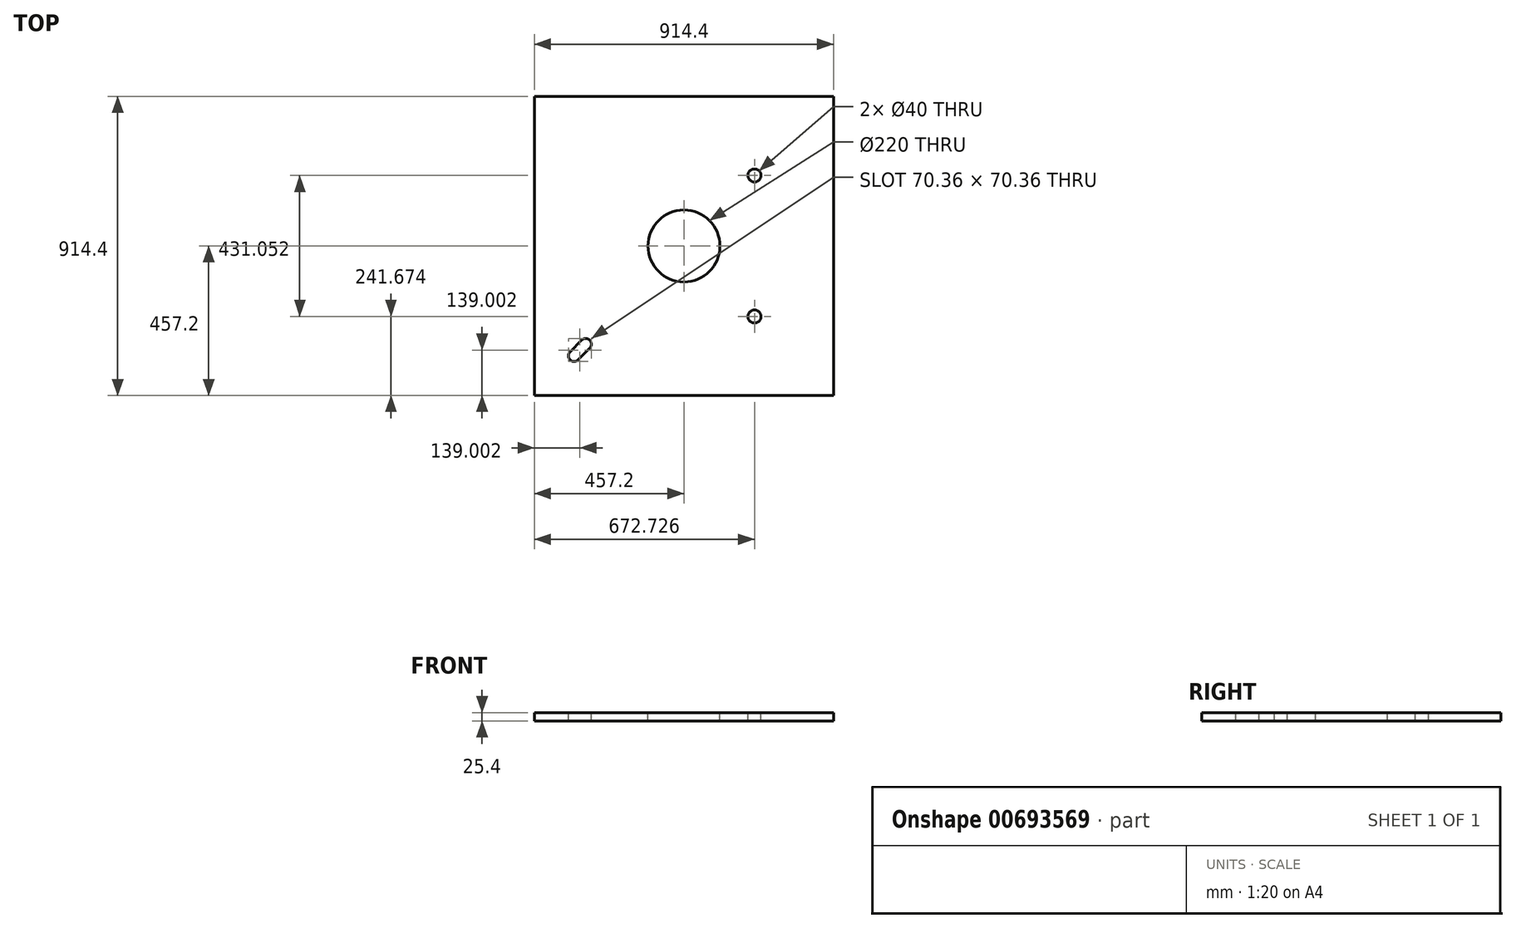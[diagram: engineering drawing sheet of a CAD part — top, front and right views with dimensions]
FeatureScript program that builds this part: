
annotation { "Feature Type Name" : "Feature", "Feature Type Description" : "" }
export const myFeature = defineFeature(function(context is Context, id is Id, definition is map)
    precondition{}
    {
        {
            var Q0;
            Q0=qCreatedBy(makeId("Top.planeOp"),FACE);
            var sketch = newSketch(context, id + "F0", { "sketchPlane" : qUnion([Q0])});
            skLineSegment(sketch, "E0.bottom", {"start": v(-457.2, 457.2) * mm, "end": v(457.2, 457.2) * mm});
            skLineSegment(sketch, "E0.top", {"start": v(-457.2, -457.2) * mm, "end": v(457.2, -457.2) * mm});
            skLineSegment(sketch, "E0.left", {"start": v(-457.2, 457.2) * mm, "end": v(-457.2, -457.2) * mm});
            skLineSegment(sketch, "E0.right", {"start": v(457.2, 457.2) * mm, "end": v(457.2, -457.2) * mm});
            skPoint(sketch, "E0.middle", {"position": v(0, 0) * mm});
            skSolve(sketch);
        }
        {
            var Q0;
            Q0=makeQuery(id+"F0.imprint","IMPRINT",FACE,{"disambiguationData":[TD([[makeQuery(id+"F0.imprint","IMPRINT",EDGE,{"derivedFrom":sQuery(id+"F0.wireOp",EDGE,"E0.bottom")}),-1.0]])]});
            extrude(context, id + "F1", {"entities" : qUnion([Q0]), "oppositeDirection" : true, "depth" : 25.4 * mm, "offsetDistance" : 25 * mm});
        }
        {
            var Q0;
            Q0=makeQuery(id+"F1.opExtrude","CAP_FACE",FACE,{"disambiguationData":[OSD([sQuery(id+"F0.wireOp",EDGE,"E0.bottom"),sQuery(id+"F0.wireOp",EDGE,"E0.top"),sQuery(id+"F0.wireOp",EDGE,"E0.left"),sQuery(id+"F0.wireOp",EDGE,"E0.right")])],"isStart":true});
            var sketch = newSketch(context, id + "F2", { "sketchPlane" : qUnion([Q0])});
            skPoint(sketch, "E1", {"position": v(0, 0) * mm});
            skSolve(sketch);
        }
        {
            var Q0;
            Q0=sQuery(id+"F2.wireOp",VERTEX,"E1");
            var Q1;
            Q1=makeQuery(id+"F1.opExtrude","SWEPT_BODY",BODY,{"disambiguationData":[OSD([sQuery(id+"F0.wireOp",EDGE,"E0.bottom"),sQuery(id+"F0.wireOp",EDGE,"E0.top"),sQuery(id+"F0.wireOp",EDGE,"E0.left"),sQuery(id+"F0.wireOp",EDGE,"E0.right")])]});
            hole(context, id + "F3", {"style" : HoleStyle.SIMPLE, "endStyle" : HoleEndStyle.THROUGH, "holeDiameter" : 220 * mm, "majorDiameter" : 5 * mm, "isTappedThrough" : true, "tappedDepth" : 12 * mm, "tapClearance" : 3, "locations" : qUnion([Q0]), "scope" : qUnion([Q1])});
        }
        {
            var Q0;
            Q0=makeQuery(id+"F1.opExtrude","CAP_FACE",FACE,{"disambiguationData":[OSD([sQuery(id+"F0.wireOp",EDGE,"E0.bottom"),sQuery(id+"F0.wireOp",EDGE,"E0.top"),sQuery(id+"F0.wireOp",EDGE,"E0.left"),sQuery(id+"F0.wireOp",EDGE,"E0.right")])],"isStart":true});
            var sketch = newSketch(context, id + "F4", { "sketchPlane" : qUnion([Q0])});
            skLineSegment(sketch, "E2.bottom", {"start": v(-215.53, 215.53) * mm, "end": v(215.53, 215.53) * mm, "construction": true});
            skLineSegment(sketch, "E2.top", {"start": v(-215.53, -215.53) * mm, "end": v(215.53, -215.53) * mm, "construction": true});
            skLineSegment(sketch, "E2.left", {"start": v(-215.53, 215.53) * mm, "end": v(-215.53, -215.53) * mm, "construction": true});
            skLineSegment(sketch, "E2.right", {"start": v(215.53, 215.53) * mm, "end": v(215.53, -215.53) * mm, "construction": true});
            skPoint(sketch, "E2.middle", {"position": v(0, 0) * mm});
            skSolve(sketch);
        }
        {
            var Q0;
            Q0=sQuery(id+"F4.wireOp",VERTEX,"E2.bottom.end");
            var Q1;
            Q1=sQuery(id+"F4.wireOp",VERTEX,"E2.right.end");
            var Q2;
            Q2=makeQuery(id+"F1.opExtrude","SWEPT_BODY",BODY,{"disambiguationData":[OSD([sQuery(id+"F0.wireOp",EDGE,"E0.bottom"),sQuery(id+"F0.wireOp",EDGE,"E0.top"),sQuery(id+"F0.wireOp",EDGE,"E0.left"),sQuery(id+"F0.wireOp",EDGE,"E0.right")])]});
            hole(context, id + "F5", {"style" : HoleStyle.SIMPLE, "endStyle" : HoleEndStyle.THROUGH, "holeDiameter" : 40 * mm, "majorDiameter" : 5 * mm, "isTappedThrough" : true, "tappedDepth" : 12 * mm, "tapClearance" : 3, "startFromSketch" : true, "locations" : qUnion([Q0, Q1]), "scope" : qUnion([Q2])});
        }
        {
            var Q0;
            Q0=makeQuery(id+"F1.opExtrude","CAP_FACE",FACE,{"disambiguationData":[OSD([sQuery(id+"F0.wireOp",EDGE,"E0.bottom"),sQuery(id+"F0.wireOp",EDGE,"E0.top"),sQuery(id+"F0.wireOp",EDGE,"E0.left"),sQuery(id+"F0.wireOp",EDGE,"E0.right")])],"isStart":true});
            var sketch = newSketch(context, id + "F6", { "sketchPlane" : qUnion([Q0])});
            skPoint(sketch, "E3", {"position": v(-335.88, -335.88) * mm});
            skLineSegment(sketch, "E4", {"start": v(0, 0) * mm, "end": v(-335.88, -335.88) * mm});
            skCircle(sketch, "E5", {"center": v(-335.88, -335.88) * mm, "radius": 17.5 * mm});
            skCircle(sketch, "E6", {"center": v(-300.52, -300.52) * mm, "radius": 17.5 * mm});
            skLineSegment(sketch, "E7", {"start": v(-312.9, -288.15) * mm, "end": v(-348.25, -323.5) * mm});
            skLineSegment(sketch, "E8", {"start": v(-288.15, -312.9) * mm, "end": v(-323.5, -348.25) * mm});
            skSolve(sketch);
        }
        {
            var Q0;
            {var subQ5=sQuery(id+"F6.wireOp",EDGE,"E8");Q0=makeQuery(id+"F6.imprint","IMPRINT",FACE,{"disambiguationData":[TD([[makeQuery(id+"F6.imprint","IMPRINT",EDGE,{"derivedFrom":subQ5}),-1.0]])]});}
            var Q1;
            {var subQ0=sQuery(id+"F6.wireOp",EDGE,"E5");var subQ1=makeQuery(id+"F6.imprint","INTERSECT",VERTEX,{"derivedFrom":[subQ0,sQuery(id+"F6.wireOp",EDGE,"E7")]});Q1=makeQuery(id+"F6.imprint","IMPRINT",FACE,{"disambiguationData":[TD([[makeQuery(id+"F6.imprint","IMPRINT",EDGE,{"disambiguationData":[TD([[subQ1,1.0]])],"derivedFrom":subQ0}),1.0]])]});}
            var Q2;
            {var subQ5=sQuery(id+"F6.wireOp",EDGE,"E7");Q2=makeQuery(id+"F6.imprint","IMPRINT",FACE,{"disambiguationData":[TD([[makeQuery(id+"F6.imprint","IMPRINT",EDGE,{"derivedFrom":subQ5}),1.0]])]});}
            var Q3;
            {var subQ0=sQuery(id+"F6.wireOp",EDGE,"E6");var subQ1=sQuery(id+"F6.wireOp",EDGE,"E4");var subQ2=makeQuery(id+"F6.imprint","INTERSECT",VERTEX,{"disambiguationData":[OD(0.0)],"derivedFrom":[subQ1,subQ0]});Q3=makeQuery(id+"F6.imprint","IMPRINT",FACE,{"disambiguationData":[TD([[makeQuery(id+"F6.imprint","IMPRINT",EDGE,{"disambiguationData":[TD([[subQ2,-1.0]])],"derivedFrom":subQ1}),1.0]])]});}
            var Q4;
            {var subQ0=sQuery(id+"F6.wireOp",EDGE,"E6");var subQ1=sQuery(id+"F6.wireOp",EDGE,"E4");var subQ2=makeQuery(id+"F6.imprint","INTERSECT",VERTEX,{"disambiguationData":[OD(0.0)],"derivedFrom":[subQ1,subQ0]});Q4=makeQuery(id+"F6.imprint","IMPRINT",FACE,{"disambiguationData":[TD([[makeQuery(id+"F6.imprint","IMPRINT",EDGE,{"disambiguationData":[TD([[subQ2,-1.0]])],"derivedFrom":subQ1}),-1.0]])]});}
            extrude(context, id + "F7", {"entities" : qUnion([Q0, Q1, Q2, Q3, Q4]), "operationType" : NewBodyOperationType.REMOVE, "endBound" : BoundingType.THROUGH_ALL, "oppositeDirection" : true, "depth" : 25 * mm, "offsetDistance" : 25 * mm});
        }
    });
